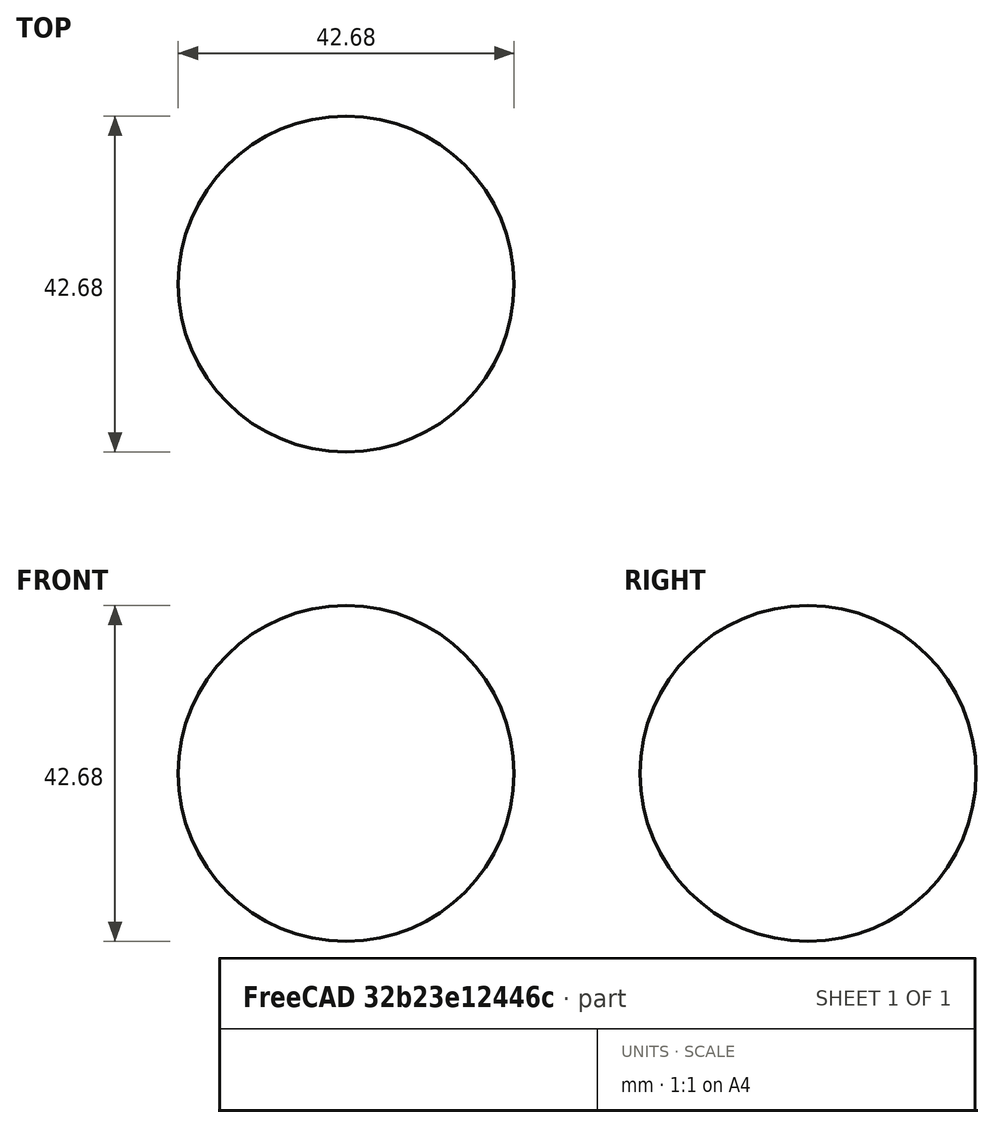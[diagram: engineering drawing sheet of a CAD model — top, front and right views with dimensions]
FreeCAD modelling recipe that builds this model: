
FCSTD DOCUMENT  (FreeCAD 1.0R39319 (Git))
Label: Golfball
License: All rights reserved
LicenseURL: https://en.wikipedia.org/wiki/All_rights_reserved
objects: PartDesign::CoordinateSystem×2, Sketcher::SketchObject×1, PartDesign::Revolution×1, PartDesign::Body×1, App::Part×1
note: 8 computed .brp shape members not serialized (recipe doc carries the construction recipe); baked Part::Feature solids carry a one-line shape summary decoded from their .brp

FEATURE [Sketcher::SketchObject] Sketch
  ArcFitTolerance = 1e-06
  AttachmentSupport = -> [XY_Plane001]
  FullyConstrained = true
  MakeInternals = false
  MapMode = 5
  sketch-geometry (2):
    g0: ArcOfCircle CenterX=0 CenterY=0 CenterZ=0 NormalX=0 NormalY=0 NormalZ=1 AngleXU=0 Radius=21.335 StartAngle=4.71239 EndAngle=7.85398
    g1: LineSegment StartX=1.6447e-12 StartY=-21.335 StartZ=0 EndX=-2.1916e-12 EndY=21.335 EndZ=0
  constraints (6):
    c: Coincident(g0,g-1)
    c: PointOnObject(g0,g-2)
    c: PointOnObject(g0,g-2)
    c: Coincident(g1,g0)
    c: Coincident(g1,g0)
    c: Radius(g0) = 21.335
FEATURE [PartDesign::Revolution] Revolution
  Angle = 360
  Angle2 = 60
  Axis = (0,1,0)
  Base = (0,0,0)
  Profile = -> Sketch
  ReferenceAxis = -> Sketch [V_Axis]
  Refine = true
  Reversed = true
  Suppressed = false
  Type = 0
FEATURE [PartDesign::Body] Body  label="Golfball001"
  AllowCompound = false
  Group = -> [Sketch,Revolution]
  Origin = -> Origin001
  Tip = -> Revolution
FEATURE [PartDesign::CoordinateSystem] center
  AttacherType = Attacher::AttachEngine3D
FEATURE [PartDesign::CoordinateSystem] floor
  AttacherType = Attacher::AttachEngine3D
  AttachmentOffset = pos=(0,0,21.335) rot=(0,0,1;0rad)
  AttachmentSupport = -> [XZ_Plane001]
  MapMode = 5
  Placement = pos=(0,-21.335,4.7e-15) rot=(1,0,0;1.5708rad)
FEATURE [App::Part] Part  label="Golfball"
  Group = -> [Body,center,floor]
  Origin = -> Origin
